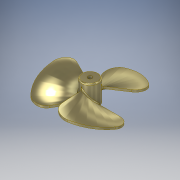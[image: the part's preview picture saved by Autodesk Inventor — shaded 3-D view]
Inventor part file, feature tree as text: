
AUTODESK INVENTOR PART (.ipt)
format: ipt  version: 2019 (Build 230136000, 136)  size: 311,808 bytes
history: native  units: mm
features: sketch x4, fillet x3, extrude x2, plane x2, helix x1, pattern_circular x1
ambient origin geometry x8: Origin, YZ Plane, XZ Plane, XY Plane, X Axis, Y Axis, Z Axis, Center Point
bodies: Solid1 (feature_tree)
feature tree (13):
  extrude  "Extrusion1"  Depth=20.0mm TaperAngle=0.0deg
  helix  "Coil1"  [1 undecoded]
  plane  "Work Plane1"
  plane  "Work Plane2"
  sketch  "Sketch3"  dims[d14=1.0mm d15=30.0mm d16=360.0deg d18=1.0mm]
  fillet  "Fillet1"  Radius=2.0mm
  fillet  "Fillet2"  Radius=10.0mm
  pattern_circular  "Circular Pattern1"  Count=3 Angle=360.0deg
  fillet  "Fillet3"  Radius=1.0mm
  extrude  "Extrusion2"  Depth=12.0mm TaperAngle=0.0deg
  sketch  "Sketch1"  dims[d0=16.0mm d1=20.0mm d2=0.0mm d3=32.0mm d4=2.0mm]
  sketch  "Sketch2"  dims[d5=50.0mm d6=12.0mm d7=10.0mm d8=0.0mm d9=90.0deg d10=90.0deg d11=0.0mm d12=0.0mm d13=10.0mm]
  sketch  "Sketch4"  dims[d19=4.0mm d20=12.0mm d21=0.0mm]
note: 1 required parameter value undecoded (feature->parameter linkage not recoverable at this tier; creation-order binding heuristic only, values carry confidence <= 0.55)
